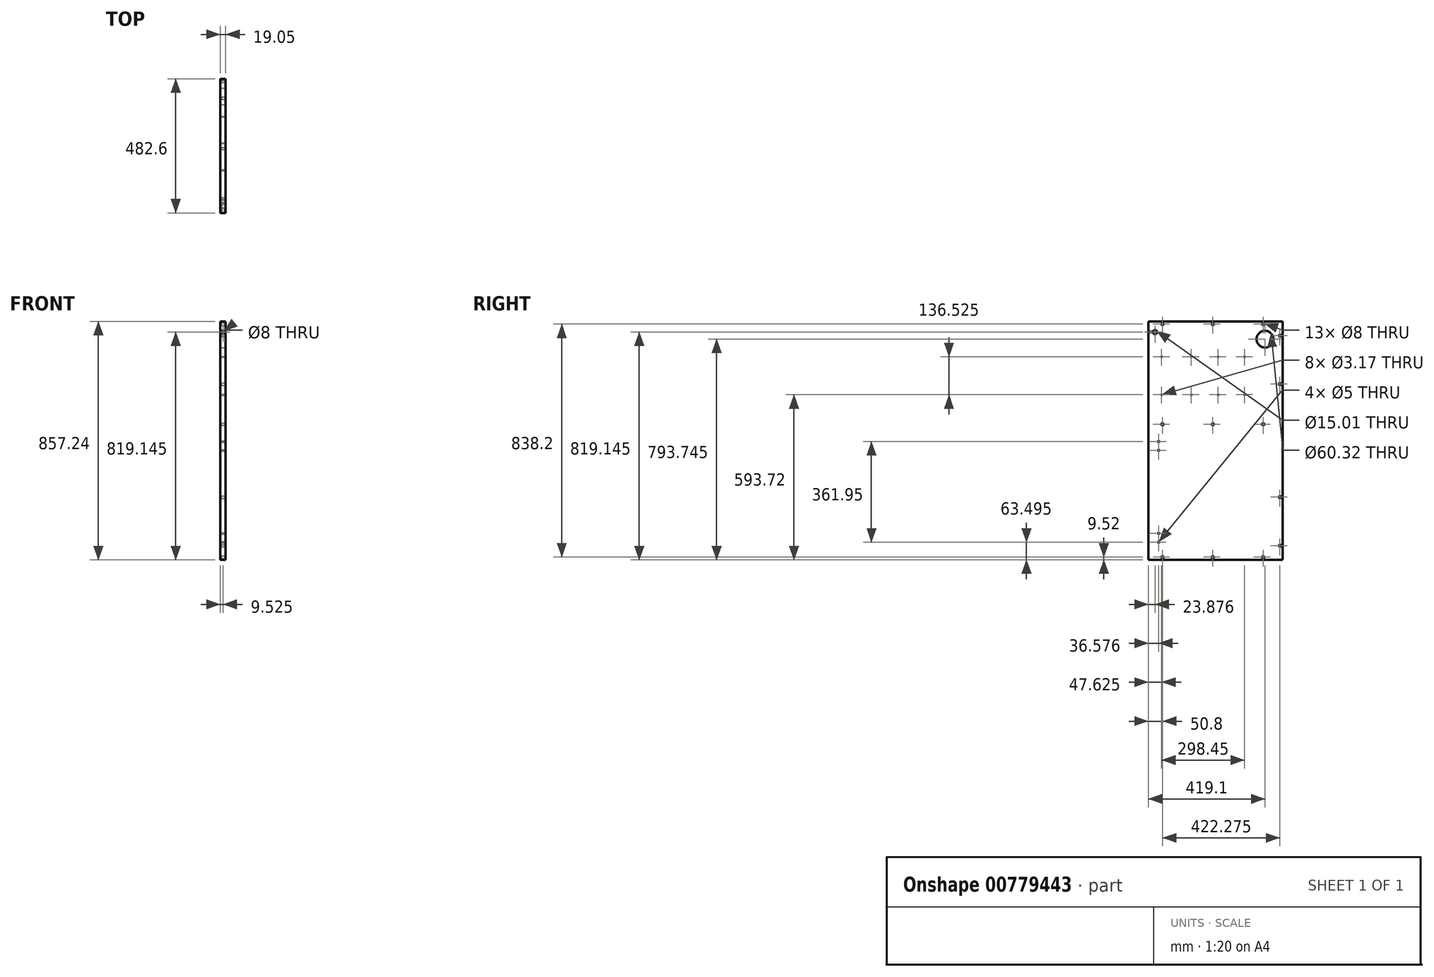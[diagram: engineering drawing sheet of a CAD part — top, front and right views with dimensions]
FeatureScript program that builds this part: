
annotation { "Feature Type Name" : "Feature", "Feature Type Description" : "" }
export const myFeature = defineFeature(function(context is Context, id is Id, definition is map)
    precondition{}
    {
        {
            var Q0;
            Q0=qCreatedBy(makeId("Right.planeOp"),FACE);
            var sketch = newSketch(context, id + "F0", { "sketchPlane" : qUnion([Q0])});
            skLineSegment(sketch, "E0.bottom", {"start": v(241.3, 428.63) * mm, "end": v(-241.3, 428.63) * mm});
            skLineSegment(sketch, "E0.top", {"start": v(241.3, -428.63) * mm, "end": v(-241.3, -428.63) * mm});
            skLineSegment(sketch, "E0.left", {"start": v(241.3, 428.63) * mm, "end": v(241.3, -428.63) * mm});
            skLineSegment(sketch, "E0.right", {"start": v(-241.3, 428.63) * mm, "end": v(-241.3, -428.63) * mm});
            skPoint(sketch, "E0.middle", {"position": v(0, 0) * mm});
            skSolve(sketch);
        }
        {
            var Q0;
            Q0=makeQuery(id+"F0.imprint","IMPRINT",FACE,{"disambiguationData":[TD([[makeQuery(id+"F0.imprint","IMPRINT",EDGE,{"derivedFrom":sQuery(id+"F0.wireOp",EDGE,"E0.bottom")}),1.0]])]});
            extrude(context, id + "F1", {"entities" : qUnion([Q0]), "depth" : 19.05 * mm, "offsetDistance" : 25.4 * mm});
        }
        {
            var Q0;
            Q0=makeQuery(id+"F1.opExtrude","CAP_FACE",FACE,{"disambiguationData":[OSD([sQuery(id+"F0.wireOp",EDGE,"E0.bottom"),sQuery(id+"F0.wireOp",EDGE,"E0.top"),sQuery(id+"F0.wireOp",EDGE,"E0.left"),sQuery(id+"F0.wireOp",EDGE,"E0.right")])],"isStart":false});
            var sketch = newSketch(context, id + "F2", { "sketchPlane" : qUnion([Q0])});
            skLineSegment(sketch, "E1", {"start": v(-241.3, 428.63) * mm, "end": v(-241.3, 419.1) * mm});
            skLineSegment(sketch, "E2", {"start": v(-241.3, 419.1) * mm, "end": v(-190.5, 419.1) * mm});
            skLineSegment(sketch, "E3", {"start": v(241.3, 428.63) * mm, "end": v(241.3, 419.1) * mm});
            skLineSegment(sketch, "E4", {"start": v(241.3, 419.1) * mm, "end": v(171.45, 419.1) * mm});
            skLineSegment(sketch, "E5", {"start": v(-241.3, 419.1) * mm, "end": v(-9.53, 419.1) * mm});
            skPoint(sketch, "E6", {"position": v(-190.5, 419.1) * mm});
            skPoint(sketch, "E7", {"position": v(-9.53, 419.1) * mm});
            skPoint(sketch, "E8", {"position": v(171.45, 419.1) * mm});
            skLineSegment(sketch, "E9", {"start": v(-241.3, -428.63) * mm, "end": v(-241.3, -419.1) * mm});
            skLineSegment(sketch, "E10", {"start": v(-241.3, -419.1) * mm, "end": v(-190.5, -419.1) * mm});
            skLineSegment(sketch, "E11", {"start": v(-241.3, -419.1) * mm, "end": v(-9.53, -419.1) * mm});
            skLineSegment(sketch, "E12", {"start": v(241.3, -428.63) * mm, "end": v(241.3, -419.1) * mm});
            skLineSegment(sketch, "E13", {"start": v(241.3, -419.1) * mm, "end": v(171.45, -419.1) * mm});
            skPoint(sketch, "E14", {"position": v(-190.5, -419.1) * mm});
            skPoint(sketch, "E15", {"position": v(-9.53, -419.1) * mm});
            skPoint(sketch, "E16", {"position": v(171.45, -419.1) * mm});
            skLineSegment(sketch, "E17", {"start": v(241.3, 428.63) * mm, "end": v(231.77, 428.63) * mm});
            skLineSegment(sketch, "E18", {"start": v(231.77, 428.63) * mm, "end": v(231.77, 377.83) * mm});
            skLineSegment(sketch, "E19", {"start": v(241.3, -428.63) * mm, "end": v(231.77, -428.63) * mm});
            skLineSegment(sketch, "E20", {"start": v(231.77, -428.63) * mm, "end": v(231.77, -377.83) * mm});
            skLineSegment(sketch, "E21", {"start": v(241.3, 0) * mm, "end": v(231.77, 0) * mm});
            skLineSegment(sketch, "E22", {"start": v(231.77, 0) * mm, "end": v(231.77, 203.2) * mm});
            skLineSegment(sketch, "E23", {"start": v(231.77, 0) * mm, "end": v(231.77, -203.2) * mm});
            skPoint(sketch, "E24", {"position": v(231.77, 203.2) * mm});
            skPoint(sketch, "E25", {"position": v(231.77, -203.2) * mm});
            skPoint(sketch, "E26", {"position": v(231.77, 377.83) * mm});
            skPoint(sketch, "E27", {"position": v(231.77, -377.83) * mm});
            skSolve(sketch);
        }
        {
            var Q0;
            Q0=sQuery(id+"F2.wireOp",VERTEX,"E6");
            var Q1;
            Q1=sQuery(id+"F2.wireOp",VERTEX,"E7");
            var Q2;
            Q2=sQuery(id+"F2.wireOp",VERTEX,"E8");
            var Q3;
            Q3=sQuery(id+"F2.wireOp",VERTEX,"E26");
            var Q4;
            Q4=sQuery(id+"F2.wireOp",VERTEX,"E24");
            var Q5;
            Q5=sQuery(id+"F2.wireOp",VERTEX,"E25");
            var Q6;
            Q6=sQuery(id+"F2.wireOp",VERTEX,"E27");
            var Q7;
            Q7=sQuery(id+"F2.wireOp",VERTEX,"E16");
            var Q8;
            Q8=sQuery(id+"F2.wireOp",VERTEX,"E15");
            var Q9;
            Q9=sQuery(id+"F2.wireOp",VERTEX,"E14");
            var Q10;
            Q10=makeQuery(id+"F1.opExtrude","SWEPT_BODY",BODY,{"disambiguationData":[OSD([sQuery(id+"F0.wireOp",EDGE,"E0.bottom"),sQuery(id+"F0.wireOp",EDGE,"E0.top"),sQuery(id+"F0.wireOp",EDGE,"E0.left"),sQuery(id+"F0.wireOp",EDGE,"E0.right")])]});
            hole(context, id + "F3", {"style" : HoleStyle.SIMPLE, "endStyle" : HoleEndStyle.BLIND, "holeDiameter" : 8 * mm, "majorDiameter" : 6.35 * mm, "holeDepth" : 14.22 * mm, "isTappedThrough" : true, "tappedDepth" : 12.7 * mm, "tapClearance" : 3, "startFromSketch" : true, "locations" : qUnion([Q0, Q1, Q2, Q3, Q4, Q5, Q6, Q7, Q8, Q9]), "scope" : qUnion([Q10])});
        }
        {
            var Q0;
            Q0=makeQuery(id+"F1.opExtrude","CAP_FACE",FACE,{"disambiguationData":[OSD([sQuery(id+"F0.wireOp",EDGE,"E0.bottom"),sQuery(id+"F0.wireOp",EDGE,"E0.top"),sQuery(id+"F0.wireOp",EDGE,"E0.left"),sQuery(id+"F0.wireOp",EDGE,"E0.right")])],"isStart":false});
            var sketch = newSketch(context, id + "F4", { "sketchPlane" : qUnion([Q0])});
            skLineSegment(sketch, "E28", {"start": v(-241.3, 428.63) * mm, "end": v(-241.3, 390.53) * mm});
            skLineSegment(sketch, "E29", {"start": v(-241.3, 390.53) * mm, "end": v(-217.42, 390.53) * mm});
            skPoint(sketch, "E30", {"position": v(-217.42, 390.53) * mm});
            skSolve(sketch);
        }
        {
            var Q0;
            Q0=sQuery(id+"F4.wireOp",VERTEX,"E29.end");
            var Q1;
            Q1=makeQuery(id+"F1.opExtrude","SWEPT_BODY",BODY,{"disambiguationData":[OSD([sQuery(id+"F0.wireOp",EDGE,"E0.bottom"),sQuery(id+"F0.wireOp",EDGE,"E0.top"),sQuery(id+"F0.wireOp",EDGE,"E0.left"),sQuery(id+"F0.wireOp",EDGE,"E0.right")])]});
            hole(context, id + "F5", {"style" : HoleStyle.SIMPLE, "endStyle" : HoleEndStyle.BLIND, "holeDiameter" : 15 * mm, "majorDiameter" : 6.35 * mm, "holeDepth" : 14.22 * mm, "isTappedThrough" : true, "tappedDepth" : 12.7 * mm, "tapClearance" : 3, "startFromSketch" : true, "locations" : qUnion([Q0]), "scope" : qUnion([Q1])});
        }
        {
            var Q0;
            Q0=makeQuery(id+"F1.opExtrude","SWEPT_FACE",FACE,{"disambiguationData":[OSD([sQuery(id+"F0.wireOp",EDGE,"E0.right")])]});
            var sketch = newSketch(context, id + "F6", { "sketchPlane" : qUnion([Q0])});
            skLineSegment(sketch, "E31", {"start": v(9.53, 428.63) * mm, "end": v(9.53, 390.53) * mm});
            skPoint(sketch, "E32", {"position": v(9.53, 390.53) * mm});
            skSolve(sketch);
        }
        {
            var Q0;
            Q0=sQuery(id+"F6.wireOp",VERTEX,"E32");
            var Q1;
            Q1=makeQuery(id+"F1.opExtrude","SWEPT_BODY",BODY,{"disambiguationData":[OSD([sQuery(id+"F0.wireOp",EDGE,"E0.bottom"),sQuery(id+"F0.wireOp",EDGE,"E0.top"),sQuery(id+"F0.wireOp",EDGE,"E0.left"),sQuery(id+"F0.wireOp",EDGE,"E0.right")])]});
            hole(context, id + "F7", {"style" : HoleStyle.SIMPLE, "endStyle" : HoleEndStyle.BLIND, "holeDiameter" : 8 * mm, "majorDiameter" : 6.35 * mm, "holeDepth" : 25.4 * mm, "isTappedThrough" : true, "tappedDepth" : 12.7 * mm, "tapClearance" : 3, "startFromSketch" : true, "locations" : qUnion([Q0]), "scope" : qUnion([Q1])});
        }
        {
            var Q0;
            Q0=makeQuery(id+"F1.opExtrude","CAP_FACE",FACE,{"disambiguationData":[OSD([sQuery(id+"F0.wireOp",EDGE,"E0.bottom"),sQuery(id+"F0.wireOp",EDGE,"E0.top"),sQuery(id+"F0.wireOp",EDGE,"E0.left"),sQuery(id+"F0.wireOp",EDGE,"E0.right")])],"isStart":false});
            var sketch = newSketch(context, id + "F8", { "sketchPlane" : qUnion([Q0])});
            skLineSegment(sketch, "E33", {"start": v(-241.3, 428.63) * mm, "end": v(-241.3, 301.63) * mm});
            skLineSegment(sketch, "E34", {"start": v(-241.3, 301.63) * mm, "end": v(-193.68, 301.63) * mm});
            skLineSegment(sketch, "E35", {"start": v(-193.68, 301.63) * mm, "end": v(-241.3, 301.63) * mm});
            skLineSegment(sketch, "E36", {"start": v(-241.3, 301.63) * mm, "end": v(-87.38, 301.63) * mm});
            skLineSegment(sketch, "E37", {"start": v(-241.3, 301.63) * mm, "end": v(9.52, 301.63) * mm});
            skLineSegment(sketch, "E38", {"start": v(-241.3, 301.63) * mm, "end": v(104.77, 301.63) * mm});
            skPoint(sketch, "E39", {"position": v(-193.68, 301.63) * mm});
            skPoint(sketch, "E40", {"position": v(-87.38, 301.63) * mm});
            skPoint(sketch, "E41", {"position": v(104.77, 301.63) * mm});
            skLineSegment(sketch, "E42", {"start": v(-241.3, 428.63) * mm, "end": v(-241.3, 269.88) * mm});
            skLineSegment(sketch, "E43", {"start": v(-241.3, 269.88) * mm, "end": v(-241.3, 60.33) * mm});
            skLineSegment(sketch, "E44", {"start": v(-241.3, 428.63) * mm, "end": v(-241.3, 352.43) * mm});
            skPoint(sketch, "E45.endSnap0", {"position": v(-241.3, 349.25) * mm});
            skLineSegment(sketch, "E46", {"start": v(-241.3, 352.43) * mm, "end": v(-241.3, 349.25) * mm});
            skLineSegment(sketch, "E47", {"start": v(-241.3, 349.25) * mm, "end": v(-241.3, 273.05) * mm});
            skLineSegment(sketch, "E48", {"start": v(-241.3, 273.05) * mm, "end": v(-241.3, 269.88) * mm});
            skLineSegment(sketch, "E49", {"start": v(-241.3, 349.25) * mm, "end": v(-241.3, 346.08) * mm});
            skLineSegment(sketch, "E50.bottom", {"start": v(-241.3, 346.08) * mm, "end": v(165.1, 346.08) * mm});
            skLineSegment(sketch, "E50.top", {"start": v(-241.3, 327.03) * mm, "end": v(165.1, 327.03) * mm});
            skLineSegment(sketch, "E50.left", {"start": v(-241.3, 346.08) * mm, "end": v(-241.3, 327.03) * mm});
            skLineSegment(sketch, "E50.right", {"start": v(165.1, 346.08) * mm, "end": v(165.1, 327.03) * mm});
            skLineSegment(sketch, "E51.top", {"start": v(-241.3, 276.23) * mm, "end": v(165.1, 276.23) * mm});
            skLineSegment(sketch, "E51.left", {"start": v(-241.3, 327.03) * mm, "end": v(-241.3, 276.23) * mm});
            skLineSegment(sketch, "E51.right", {"start": v(165.1, 327.03) * mm, "end": v(165.1, 276.23) * mm});
            skLineSegment(sketch, "E52", {"start": v(-241.3, 165.1) * mm, "end": v(-193.68, 165.1) * mm});
            skLineSegment(sketch, "E53", {"start": v(-241.3, 165.1) * mm, "end": v(-87.38, 165.1) * mm});
            skLineSegment(sketch, "E54", {"start": v(-241.3, 165.1) * mm, "end": v(9.52, 165.1) * mm});
            skLineSegment(sketch, "E55", {"start": v(-241.3, 165.1) * mm, "end": v(104.77, 165.1) * mm});
            skPoint(sketch, "E56", {"position": v(-193.68, 165.1) * mm});
            skPoint(sketch, "E57", {"position": v(-87.38, 165.1) * mm});
            skPoint(sketch, "E58", {"position": v(9.52, 165.1) * mm});
            skPoint(sketch, "E59", {"position": v(104.77, 165.1) * mm});
            skLineSegment(sketch, "E60", {"start": v(-241.3, 60.33) * mm, "end": v(-241.3, 57.15) * mm});
            skLineSegment(sketch, "E61", {"start": v(-241.3, 57.15) * mm, "end": v(-241.3, -428.63) * mm});
            skLineSegment(sketch, "E62", {"start": v(-241.3, 57.15) * mm, "end": v(-241.3, -19.05) * mm});
            skLineSegment(sketch, "E63", {"start": v(-241.3, -19.05) * mm, "end": v(-204.72, -19.05) * mm});
            skLineSegment(sketch, "E64", {"start": v(-204.72, -19.05) * mm, "end": v(-204.72, -3.17) * mm});
            skLineSegment(sketch, "E65", {"start": v(-204.72, -3.17) * mm, "end": v(-204.72, -34.92) * mm});
            skPoint(sketch, "E65.endSnap0", {"position": v(-204.72, -11.11) * mm});
            skPoint(sketch, "E66", {"position": v(-204.72, -3.17) * mm});
            skPoint(sketch, "E67", {"position": v(-204.72, -34.92) * mm});
            skLineSegment(sketch, "E68", {"start": v(-241.3, 57.15) * mm, "end": v(-241.3, -349.25) * mm});
            skLineSegment(sketch, "E69", {"start": v(-241.3, -349.25) * mm, "end": v(-204.72, -349.25) * mm});
            skLineSegment(sketch, "E70", {"start": v(-204.72, -349.25) * mm, "end": v(-204.72, -333.38) * mm});
            skLineSegment(sketch, "E71", {"start": v(-204.72, -333.38) * mm, "end": v(-204.72, -365.12) * mm});
            skPoint(sketch, "E72", {"position": v(-204.72, -333.38) * mm});
            skPoint(sketch, "E73", {"position": v(-204.72, -365.12) * mm});
            skLineSegment(sketch, "E74", {"start": v(-241.3, 58.74) * mm, "end": v(-190.5, 58.74) * mm});
            skLineSegment(sketch, "E75", {"start": v(-190.5, 58.74) * mm, "end": v(171.45, 58.74) * mm});
            skLineSegment(sketch, "E76", {"start": v(-241.3, 58.74) * mm, "end": v(-9.53, 58.74) * mm});
            skPoint(sketch, "E77", {"position": v(-190.5, 58.74) * mm});
            skPoint(sketch, "E78", {"position": v(-9.53, 58.74) * mm});
            skPoint(sketch, "E79", {"position": v(171.45, 58.74) * mm});
            skSolve(sketch);
        }
        {
            var Q0;
            Q0=sQuery(id+"F8.wireOp",VERTEX,"E39");
            var Q1;
            Q1=sQuery(id+"F8.wireOp",VERTEX,"E40");
            var Q2;
            Q2=sQuery(id+"F8.wireOp",VERTEX,"E41");
            var Q3;
            Q3=sQuery(id+"F8.wireOp",VERTEX,"E59");
            var Q4;
            Q4=sQuery(id+"F8.wireOp",VERTEX,"E58");
            var Q5;
            Q5=sQuery(id+"F8.wireOp",VERTEX,"E57");
            var Q6;
            Q6=sQuery(id+"F8.wireOp",VERTEX,"E37.end");
            var Q7;
            Q7=sQuery(id+"F8.wireOp",VERTEX,"E56");
            var Q8;
            Q8=makeQuery(id+"F1.opExtrude","SWEPT_BODY",BODY,{"disambiguationData":[OSD([sQuery(id+"F0.wireOp",EDGE,"E0.bottom"),sQuery(id+"F0.wireOp",EDGE,"E0.top"),sQuery(id+"F0.wireOp",EDGE,"E0.left"),sQuery(id+"F0.wireOp",EDGE,"E0.right")])]});
            hole(context, id + "F9", {"style" : HoleStyle.SIMPLE, "endStyle" : HoleEndStyle.BLIND, "holeDiameter" : 3.17 * mm, "majorDiameter" : 6.35 * mm, "holeDepth" : 14.22 * mm, "isTappedThrough" : true, "tappedDepth" : 12.7 * mm, "tapClearance" : 3, "startFromSketch" : true, "locations" : qUnion([Q0, Q1, Q2, Q3, Q4, Q5, Q6, Q7]), "scope" : qUnion([Q8])});
        }
        {
            var Q0;
            Q0=sQuery(id+"F8.wireOp",VERTEX,"E66");
            var Q1;
            Q1=sQuery(id+"F8.wireOp",VERTEX,"E67");
            var Q2;
            Q2=sQuery(id+"F8.wireOp",VERTEX,"E72");
            var Q3;
            Q3=sQuery(id+"F8.wireOp",VERTEX,"E73");
            var Q4;
            Q4=makeQuery(id+"F1.opExtrude","SWEPT_BODY",BODY,{"disambiguationData":[OSD([sQuery(id+"F0.wireOp",EDGE,"E0.bottom"),sQuery(id+"F0.wireOp",EDGE,"E0.top"),sQuery(id+"F0.wireOp",EDGE,"E0.left"),sQuery(id+"F0.wireOp",EDGE,"E0.right")])]});
            hole(context, id + "F10", {"style" : HoleStyle.SIMPLE, "endStyle" : HoleEndStyle.BLIND, "holeDiameter" : 5 * mm, "majorDiameter" : 6.35 * mm, "holeDepth" : 14.22 * mm, "isTappedThrough" : true, "tappedDepth" : 12.7 * mm, "tapClearance" : 3, "startFromSketch" : true, "locations" : qUnion([Q0, Q1, Q2, Q3]), "scope" : qUnion([Q4])});
        }
        {
            var Q0;
            Q0=makeQuery(id+"F1.opExtrude","CAP_FACE",FACE,{"disambiguationData":[OSD([sQuery(id+"F0.wireOp",EDGE,"E0.bottom"),sQuery(id+"F0.wireOp",EDGE,"E0.top"),sQuery(id+"F0.wireOp",EDGE,"E0.left"),sQuery(id+"F0.wireOp",EDGE,"E0.right")])],"isStart":false});
            var sketch = newSketch(context, id + "F11", { "sketchPlane" : qUnion([Q0])});
            skLineSegment(sketch, "E80", {"start": v(241.3, 428.63) * mm, "end": v(177.8, 428.63) * mm});
            skLineSegment(sketch, "E81", {"start": v(177.8, 428.63) * mm, "end": v(177.8, 365.13) * mm});
            skCircle(sketch, "E82", {"center": v(177.8, 365.13) * mm, "radius": 30.16 * mm});
            skSolve(sketch);
        }
        {
            var Q0;
            Q0=makeQuery(id+"F11.imprint","IMPRINT",FACE,{"disambiguationData":[TD([[makeQuery(id+"F11.imprint","IMPRINT",EDGE,{"derivedFrom":sQuery(id+"F11.wireOp",EDGE,"E82")}),1.0]])]});
            extrude(context, id + "F12", {"entities" : qUnion([Q0]), "operationType" : NewBodyOperationType.REMOVE, "oppositeDirection" : true, "depth" : 25.4 * mm, "offsetDistance" : 25.4 * mm});
        }
        {
            var Q0;
            Q0=sQuery(id+"F8.wireOp",VERTEX,"E77");
            var Q1;
            Q1=sQuery(id+"F8.wireOp",VERTEX,"E78");
            var Q2;
            Q2=sQuery(id+"F8.wireOp",VERTEX,"E79");
            var Q3;
            Q3=makeQuery(id+"F1.opExtrude","SWEPT_BODY",BODY,{"disambiguationData":[OSD([sQuery(id+"F0.wireOp",EDGE,"E0.bottom"),sQuery(id+"F0.wireOp",EDGE,"E0.top"),sQuery(id+"F0.wireOp",EDGE,"E0.left"),sQuery(id+"F0.wireOp",EDGE,"E0.right")])]});
            hole(context, id + "F13", {"style" : HoleStyle.SIMPLE, "endStyle" : HoleEndStyle.BLIND, "holeDiameter" : 8 * mm, "majorDiameter" : 6.35 * mm, "holeDepth" : 14.22 * mm, "isTappedThrough" : true, "tappedDepth" : 12.7 * mm, "tapClearance" : 3, "startFromSketch" : true, "locations" : qUnion([Q0, Q1, Q2]), "scope" : qUnion([Q3])});
        }
    });
